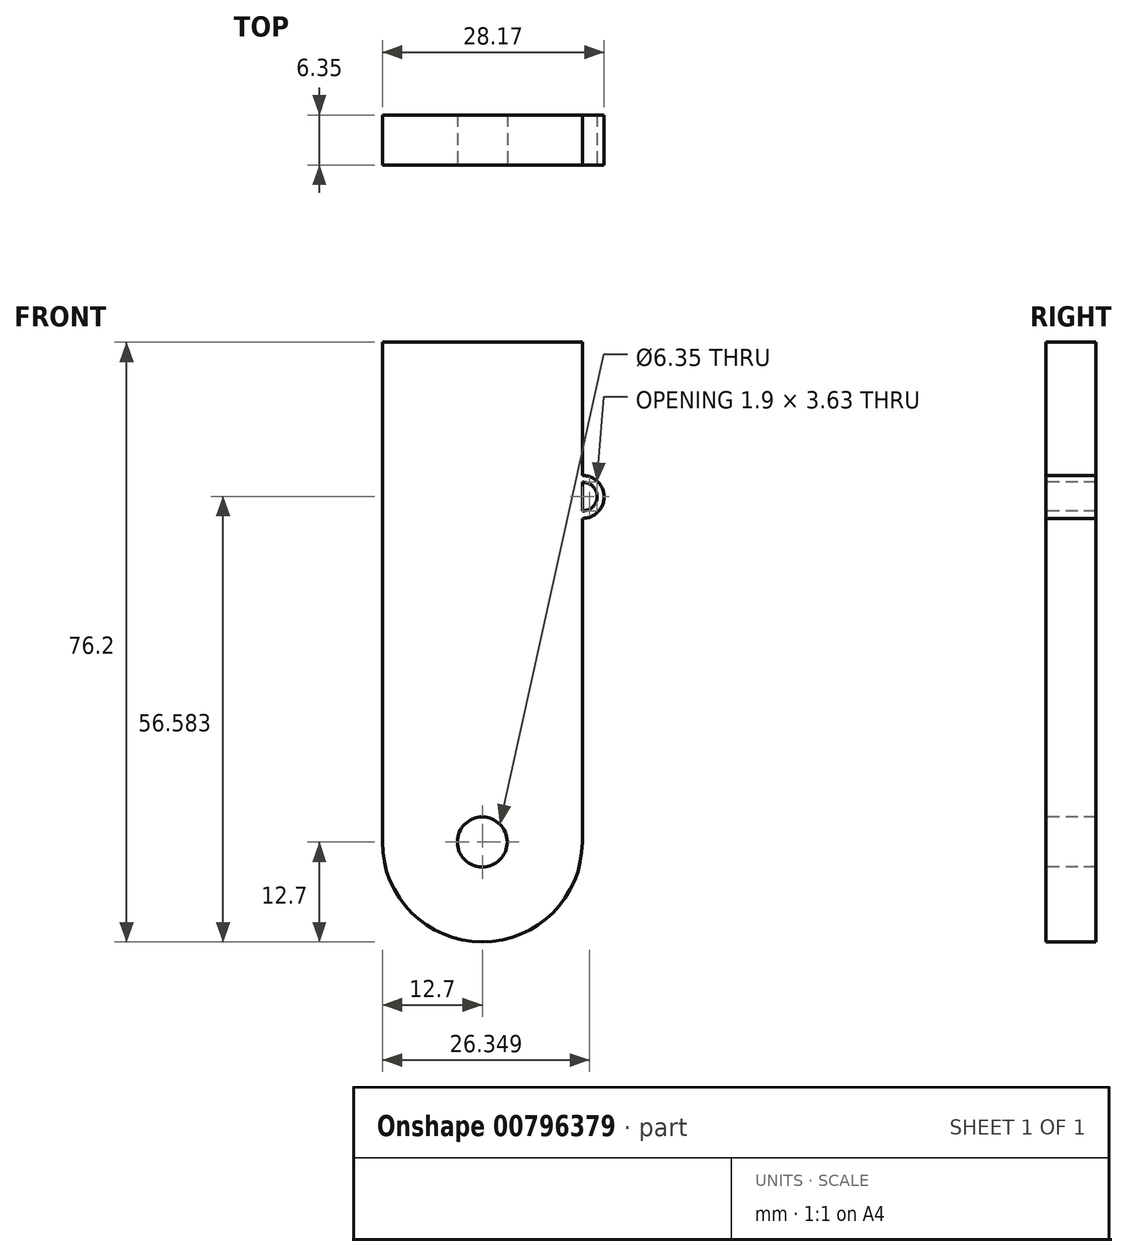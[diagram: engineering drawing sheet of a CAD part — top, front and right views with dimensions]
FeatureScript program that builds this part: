
annotation { "Feature Type Name" : "Feature", "Feature Type Description" : "" }
export const myFeature = defineFeature(function(context is Context, id is Id, definition is map)
    precondition{}
    {
        {
            var Q0;
            Q0=qCreatedBy(makeId("Front.planeOp"),FACE);
            var sketch = newSketch(context, id + "F0", { "sketchPlane" : qUnion([Q0])});
            skLineSegment(sketch, "E0.bottom", {"start": v(0, 0) * mm, "end": v(25.4, 0) * mm});
            skLineSegment(sketch, "E0.top", {"start": v(0, 63.5) * mm, "end": v(25.4, 63.5) * mm});
            skLineSegment(sketch, "E0.left", {"start": v(0, 0) * mm, "end": v(0, 63.5) * mm});
            skLineSegment(sketch, "E0.right", {"start": v(25.4, 0) * mm, "end": v(25.4, 63.5) * mm});
            skArc(sketch, "E1", {"start": v(0, 0) * mm, "mid": v(12.7, -12.7) * mm, "end": v(25.4, 0) * mm});
            skSolve(sketch);
        }
        {
            var Q0;
            Q0 = qSketchRegion(id + "F0", true);
            extrude(context, id + "F1", {"entities" : qUnion([Q0]), "depth" : 6.35 * mm, "offsetDistance" : 25.4 * mm});
        }
        {
            var Q0;
            Q0=makeQuery(id+"F1.opExtrude","CAP_FACE",FACE,{"disambiguationData":[OSD([sQuery(id+"F0.wireOp",EDGE,"E0.top"),sQuery(id+"F0.wireOp",EDGE,"E0.left"),sQuery(id+"F0.wireOp",EDGE,"E0.right"),sQuery(id+"F0.wireOp",EDGE,"E1")])],"isStart":false});
            var sketch = newSketch(context, id + "F2", { "sketchPlane" : qUnion([Q0])});
            skCircle(sketch, "E2", {"center": v(12.7, 0) * mm, "radius": 3.18 * mm});
            skSolve(sketch);
        }
        {
            var Q0;
            Q0=makeQuery(id+"F2.imprint","IMPRINT",FACE,{"disambiguationData":[TD([[makeQuery(id+"F2.imprint","IMPRINT",EDGE,{"derivedFrom":sQuery(id+"F2.wireOp",EDGE,"E2")}),1.0]])]});
            extrude(context, id + "F3", {"entities" : qUnion([Q0]), "operationType" : NewBodyOperationType.REMOVE, "endBound" : BoundingType.UP_TO_NEXT, "oppositeDirection" : true, "depth" : 25.4 * mm, "offsetDistance" : 25.4 * mm});
        }
        {
            var Q0;
            Q0=makeQuery(id+"F1.opExtrude","CAP_FACE",FACE,{"disambiguationData":[OSD([sQuery(id+"F0.wireOp",EDGE,"E0.top"),sQuery(id+"F0.wireOp",EDGE,"E0.left"),sQuery(id+"F0.wireOp",EDGE,"E0.right"),sQuery(id+"F0.wireOp",EDGE,"E1")])],"isStart":false});
            var sketch = newSketch(context, id + "F4", { "sketchPlane" : qUnion([Q0])});
            skArc(sketch, "E3", {"start": v(25.4, 41.12) * mm, "mid": v(28.17, 43.83) * mm, "end": v(25.4, 46.55) * mm});
            skArc(sketch, "E4", {"start": v(25.4, 42.07) * mm, "mid": v(27.3, 43.88) * mm, "end": v(25.4, 45.7) * mm});
            skLineSegment(sketch, "E5", {"start": v(25.4, 45.7) * mm, "end": v(25.4, 46.55) * mm});
            skLineSegment(sketch, "E6", {"start": v(25.4, 42.07) * mm, "end": v(25.4, 41.12) * mm});
            skSolve(sketch);
        }
        {
            var Q0;
            Q0=makeQuery(id+"F4.imprint","IMPRINT",FACE,{"disambiguationData":[TD([[makeQuery(id+"F4.imprint","IMPRINT",EDGE,{"derivedFrom":sQuery(id+"F4.wireOp",EDGE,"E3")}),1.0]])]});
            var Q1;
            Q1=makeQuery(id+"F1.opExtrude","CAP_FACE",FACE,{"disambiguationData":[OSD([sQuery(id+"F0.wireOp",EDGE,"E0.top"),sQuery(id+"F0.wireOp",EDGE,"E0.left"),sQuery(id+"F0.wireOp",EDGE,"E0.right"),sQuery(id+"F0.wireOp",EDGE,"E1")])],"isStart":true});
            extrude(context, id + "F5", {"entities" : qUnion([Q0]), "operationType" : NewBodyOperationType.ADD, "endBound" : BoundingType.UP_TO_SURFACE, "oppositeDirection" : true, "depth" : 25.4 * mm, "endBoundEntityFace" : qUnion([Q1]), "offsetDistance" : 25.4 * mm});
        }
    });
